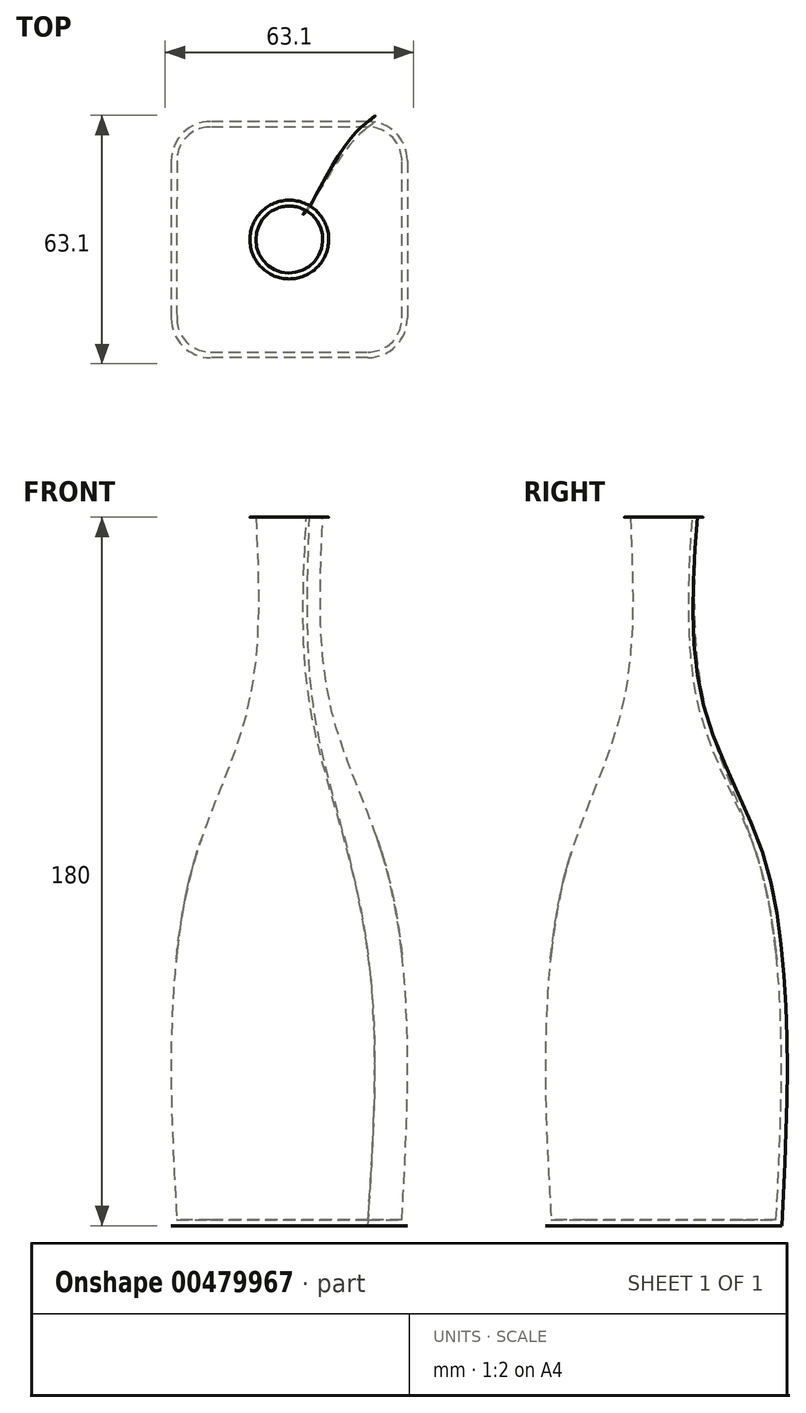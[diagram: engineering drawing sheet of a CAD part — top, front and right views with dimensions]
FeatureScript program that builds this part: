
annotation { "Feature Type Name" : "Feature", "Feature Type Description" : "" }
export const myFeature = defineFeature(function(context is Context, id is Id, definition is map)
    precondition{}
    {
        {
            var Q0;
            Q0=qCreatedBy(makeId("Top.planeOp"),FACE);
            var sketch = newSketch(context, id + "F0", { "sketchPlane" : qUnion([Q0])});
            skLineSegment(sketch, "E0.bottom", {"start": v(20, 30) * mm, "end": v(-20, 30) * mm});
            skLineSegment(sketch, "E0.top", {"start": v(20, -30) * mm, "end": v(-20, -30) * mm});
            skLineSegment(sketch, "E0.left", {"start": v(30, 20) * mm, "end": v(30, -20) * mm});
            skLineSegment(sketch, "E0.right", {"start": v(-30, 20) * mm, "end": v(-30, -20) * mm});
            skPoint(sketch, "E0.middle", {"position": v(0, 0) * mm});
            skPoint(sketch, "E1.visualSharp", {"position": v(-30, 30) * mm});
            skArc(sketch, "E1.filletArc", {"start": v(-20, 30) * mm, "mid": v(-27.07, 27.07) * mm, "end": v(-30, 20) * mm});
            skPoint(sketch, "E2.visualSharp", {"position": v(30, 30) * mm});
            skArc(sketch, "E2.filletArc", {"start": v(30, 20) * mm, "mid": v(27.07, 27.07) * mm, "end": v(20, 30) * mm});
            skPoint(sketch, "E3.visualSharp", {"position": v(30, -30) * mm});
            skArc(sketch, "E3.filletArc", {"start": v(20, -30) * mm, "mid": v(27.07, -27.07) * mm, "end": v(30, -20) * mm});
            skPoint(sketch, "E4.visualSharp", {"position": v(-30, -30) * mm});
            skArc(sketch, "E4.filletArc", {"start": v(-30, -20) * mm, "mid": v(-27.07, -27.07) * mm, "end": v(-20, -30) * mm});
            skSolve(sketch);
        }
        {
            var Q0;
            Q0=makeQuery(id+"F0.imprint","IMPRINT",FACE,{"disambiguationData":[TD([[makeQuery(id+"F0.imprint","IMPRINT",EDGE,{"derivedFrom":sQuery(id+"F0.wireOp",EDGE,"E0.bottom")}),1.0]])]});
            cPlane(context, id + "F1", {"entities" : qUnion([Q0]), "cplaneType" : CPlaneType.OFFSET, "offset" : 70 * mm, "width" : 150 * mm, "height" : 150 * mm});
        }
        {
            var Q0;
            Q0=qCreatedBy(id+"F1.planeOp",FACE);
            var sketch = newSketch(context, id + "F2", { "sketchPlane" : qUnion([Q0])});
            skLineSegment(sketch, "E5.bottom", {"start": v(20, 30) * mm, "end": v(-20, 30) * mm});
            skLineSegment(sketch, "E5.top", {"start": v(20, -30) * mm, "end": v(-20, -30) * mm});
            skLineSegment(sketch, "E5.left", {"start": v(30, 20) * mm, "end": v(30, -20) * mm});
            skLineSegment(sketch, "E5.right", {"start": v(-30, 20) * mm, "end": v(-30, -20) * mm});
            skPoint(sketch, "E5.middle", {"position": v(0, 0) * mm});
            skPoint(sketch, "E6.visualSharp", {"position": v(-30, 30) * mm});
            skArc(sketch, "E6.filletArc", {"start": v(-20, 30) * mm, "mid": v(-27.07, 27.07) * mm, "end": v(-30, 20) * mm});
            skPoint(sketch, "E7.visualSharp", {"position": v(30, 30) * mm});
            skArc(sketch, "E7.filletArc", {"start": v(30, 20) * mm, "mid": v(27.07, 27.07) * mm, "end": v(20, 30) * mm});
            skPoint(sketch, "E8.visualSharp", {"position": v(-30, -30) * mm});
            skArc(sketch, "E8.filletArc", {"start": v(-30, -20) * mm, "mid": v(-27.07, -27.07) * mm, "end": v(-20, -30) * mm});
            skPoint(sketch, "E9.visualSharp", {"position": v(30, -30) * mm});
            skArc(sketch, "E9.filletArc", {"start": v(20, -30) * mm, "mid": v(27.07, -27.07) * mm, "end": v(30, -20) * mm});
            skSolve(sketch);
        }
        {
            var Q0;
            Q0=makeQuery(id+"F2.imprint","IMPRINT",FACE,{"disambiguationData":[TD([[makeQuery(id+"F2.imprint","IMPRINT",EDGE,{"derivedFrom":sQuery(id+"F2.wireOp",EDGE,"E5.bottom")}),1.0]])]});
            cPlane(context, id + "F3", {"entities" : qUnion([Q0]), "cplaneType" : CPlaneType.OFFSET, "offset" : 25 * mm, "width" : 150 * mm, "height" : 150 * mm});
        }
        {
            var Q0;
            Q0=qCreatedBy(id+"F3.planeOp",FACE);
            var sketch = newSketch(context, id + "F4", { "sketchPlane" : qUnion([Q0])});
            skLineSegment(sketch, "E10.bottom", {"start": v(15, 25) * mm, "end": v(-15, 25) * mm});
            skLineSegment(sketch, "E10.top", {"start": v(15, -25) * mm, "end": v(-15, -25) * mm});
            skLineSegment(sketch, "E10.left", {"start": v(25, 15) * mm, "end": v(25, -15) * mm});
            skLineSegment(sketch, "E10.right", {"start": v(-25, 15) * mm, "end": v(-25, -15) * mm});
            skPoint(sketch, "E10.middle", {"position": v(0, 0) * mm});
            skPoint(sketch, "E11.visualSharp", {"position": v(-25, 25) * mm});
            skArc(sketch, "E11.filletArc", {"start": v(-15, 25) * mm, "mid": v(-22.07, 22.07) * mm, "end": v(-25, 15) * mm});
            skPoint(sketch, "E12.visualSharp", {"position": v(25, 25) * mm});
            skArc(sketch, "E12.filletArc", {"start": v(25, 15) * mm, "mid": v(22.07, 22.07) * mm, "end": v(15, 25) * mm});
            skPoint(sketch, "E13.visualSharp", {"position": v(25, -25) * mm});
            skArc(sketch, "E13.filletArc", {"start": v(15, -25) * mm, "mid": v(22.07, -22.07) * mm, "end": v(25, -15) * mm});
            skPoint(sketch, "E14.visualSharp", {"position": v(-25, -25) * mm});
            skArc(sketch, "E14.filletArc", {"start": v(-25, -15) * mm, "mid": v(-22.07, -22.07) * mm, "end": v(-15, -25) * mm});
            skSolve(sketch);
        }
        {
            var Q0;
            Q0=makeQuery(id+"F4.imprint","IMPRINT",FACE,{"disambiguationData":[TD([[makeQuery(id+"F4.imprint","IMPRINT",EDGE,{"derivedFrom":sQuery(id+"F4.wireOp",EDGE,"E10.bottom")}),1.0]])]});
            cPlane(context, id + "F5", {"entities" : qUnion([Q0]), "cplaneType" : CPlaneType.OFFSET, "offset" : 35 * mm, "width" : 150 * mm, "height" : 150 * mm});
        }
        {
            var Q0;
            Q0=qCreatedBy(id+"F5.planeOp",FACE);
            var sketch = newSketch(context, id + "F6", { "sketchPlane" : qUnion([Q0])});
            skCircle(sketch, "E15", {"center": v(0, 0) * mm, "radius": 12.5 * mm});
            skSolve(sketch);
        }
        {
            var Q0;
            Q0=qCreatedBy(id+"F5.planeOp",FACE);
            cPlane(context, id + "F7", {"entities" : qUnion([Q0]), "cplaneType" : CPlaneType.OFFSET, "offset" : 50 * mm, "width" : 150 * mm, "height" : 150 * mm});
        }
        {
            var Q0;
            Q0=qCreatedBy(id+"F7.planeOp",FACE);
            var sketch = newSketch(context, id + "F8", { "sketchPlane" : qUnion([Q0])});
            skCircle(sketch, "E16", {"center": v(0, 0) * mm, "radius": 10 * mm});
            skSolve(sketch);
        }
        {
            var Q0;
            Q0=makeQuery(id+"F0.imprint","IMPRINT",FACE,{"disambiguationData":[TD([[makeQuery(id+"F0.imprint","IMPRINT",EDGE,{"derivedFrom":sQuery(id+"F0.wireOp",EDGE,"E0.bottom")}),1.0]])]});
            var Q1;
            Q1=makeQuery(id+"F2.imprint","IMPRINT",FACE,{"disambiguationData":[TD([[makeQuery(id+"F2.imprint","IMPRINT",EDGE,{"derivedFrom":sQuery(id+"F2.wireOp",EDGE,"E5.bottom")}),1.0]])]});
            var Q2;
            Q2=makeQuery(id+"F4.imprint","IMPRINT",FACE,{"disambiguationData":[TD([[makeQuery(id+"F4.imprint","IMPRINT",EDGE,{"derivedFrom":sQuery(id+"F4.wireOp",EDGE,"E10.bottom")}),1.0]])]});
            var Q3;
            Q3=makeQuery(id+"F6.imprint","IMPRINT",FACE,{"disambiguationData":[TD([[makeQuery(id+"F6.imprint","IMPRINT",EDGE,{"derivedFrom":sQuery(id+"F6.wireOp",EDGE,"E15")}),1.0]])]});
            var Q4;
            Q4=makeQuery(id+"F8.imprint","IMPRINT",FACE,{"disambiguationData":[TD([[makeQuery(id+"F8.imprint","IMPRINT",EDGE,{"derivedFrom":sQuery(id+"F8.wireOp",EDGE,"E16")}),1.0]])]});
            loft(context, id + "F9", {"sheetProfilesArray" : [{ "sheetProfileEntities" : qUnion([Q0]) }, { "sheetProfileEntities" : qUnion([Q1]) }, { "sheetProfileEntities" : qUnion([Q2]) }, { "sheetProfileEntities" : qUnion([Q3]) }, { "sheetProfileEntities" : qUnion([Q4]) }]});
        }
        {
            var Q0;
            Q0=makeQuery(id+"F9.opLoft","CAP_FACE",FACE,{"disambiguationData":[OSD([makeQuery(id+"F8.imprint","IMPRINT",FACE,{"disambiguationData":[TD([[makeQuery(id+"F8.imprint","IMPRINT",EDGE,{"derivedFrom":sQuery(id+"F8.wireOp",EDGE,"E16")}),1.0]])]})])],"isStart":true});
            shell(context, id + "F10", {"entities" : qUnion([Q0]), "thickness" : 1.5 * mm});
        }
    });
